# Revit family: Кресло мягкое
name_source: partatom
category: Оборудование
revit_build: Autodesk Revit 2017 (Build: 20170118_1100(x64)
units: mm (PartAtom-declared; Revit-internal decimal feet)

## family parameters
Всегда вертикально = Да
На основе рабочей плоскости = Нет
Общий = Нет
При загрузке вырезать с полостями = Нет
Размер круглого соединителя = Использовать диаметр
Тип детали = Нормальный
Точка расчета площади = Нет

## types (3) — shared parameters

## per-type parameters (varying)
| type | Изготовитель | Общ_Высота | Общ_Глубина | Общ_Единицы измерения | Общ_Наименование | Общ_Поставщик | Общ_Тип, марка | Общ_Ширина |
| Chairman Симпл 820х830х830 | Severin | 830 мм | 830 мм |  | Кресло мягкое | Chairman | Симпл | 820 мм |
| Диван мягкий трехместный |  | 870 мм | 950 мм |  | Диван мягкий трехместный | Меб-фф, Россия | Арт: Chairman Симпл /3 | 1930 мм |
| Диван двухместный |  | 800 мм | 870 мм | шт. | Диван двухместный |  |  | 1830 мм |

## geometry (parser evidence)
native form markers: Sweep x1
no freeform markers — native parametric forms only
